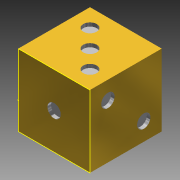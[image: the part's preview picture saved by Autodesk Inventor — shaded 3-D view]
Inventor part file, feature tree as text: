
AUTODESK INVENTOR PART (.ipt)
format: ipt  version: 2013 (Build 170138000, 138)  size: 207,872 bytes
history: native  units: in
note: dims shown in document units (in); Inventor stores cm internally (conversion verified against a paired STEP export)
features: sketch x8, extrude x7
ambient origin geometry x8: Origin, YZ Plane, XZ Plane, XY Plane, X Axis, Y Axis, Z Axis, Center Point
bodies: Solid1 (feature_tree)
feature tree (15):
  extrude  "Extrusion1"  Depth=1.0in
  sketch  "Sketch2"  dims[d2=1.0in d3=0.0in d4=0.187in]
  sketch  "Sketch3"  dims[d5=0.05in d6=0.0in d7=0.187in]
  extrude  "Extrusion2"  Depth=0.187in
  extrude  "Extrusion3"  Depth=0.187in
  extrude  "Extrusion4"  Depth=0.187in
  extrude  "Extrusion5"  Depth=0.187in
  extrude  "Extrusion6"  Depth=0.187in
  extrude  "Extrusion7"  Depth=0.05in TaperAngle=0.0deg
  sketch  "Sketch1"  dims[d0=1.0in d1=1.0in]
  sketch  "Sketch4"  dims[d8=0.187in d9=0.187in]
  sketch  "Sketch5"  dims[d10=0.05in d11=0.0in d12=0.187in]
  sketch  "Sketch6"  dims[d13=0.187in d14=0.187in]
  sketch  "Sketch7"  dims[d15=0.187in d16=0.05in d17=0.0in]
  sketch  "Sketch8"  dims[d18=0.187in d19=0.187in d20=0.187in d21=0.187in d22=0.187in d23=0.187in d24=0.05in d25=0.0in d26=0.25in d27=0.25in d28=0.25in d29=0.2498in d30=0.25in d31=0.2498in d32=0.25in d33=0.25in d34=0.5in d35=0.5in d36=0.187in d37=0.187in d38=0.187in d39=0.187in d40=0.187in d41=0.05in d42=0.0in d43=0.187in d44=0.187in d45=0.25in d46=0.25in d47=0.25in d48=0.25in d49=0.05in d50=0.0in]
